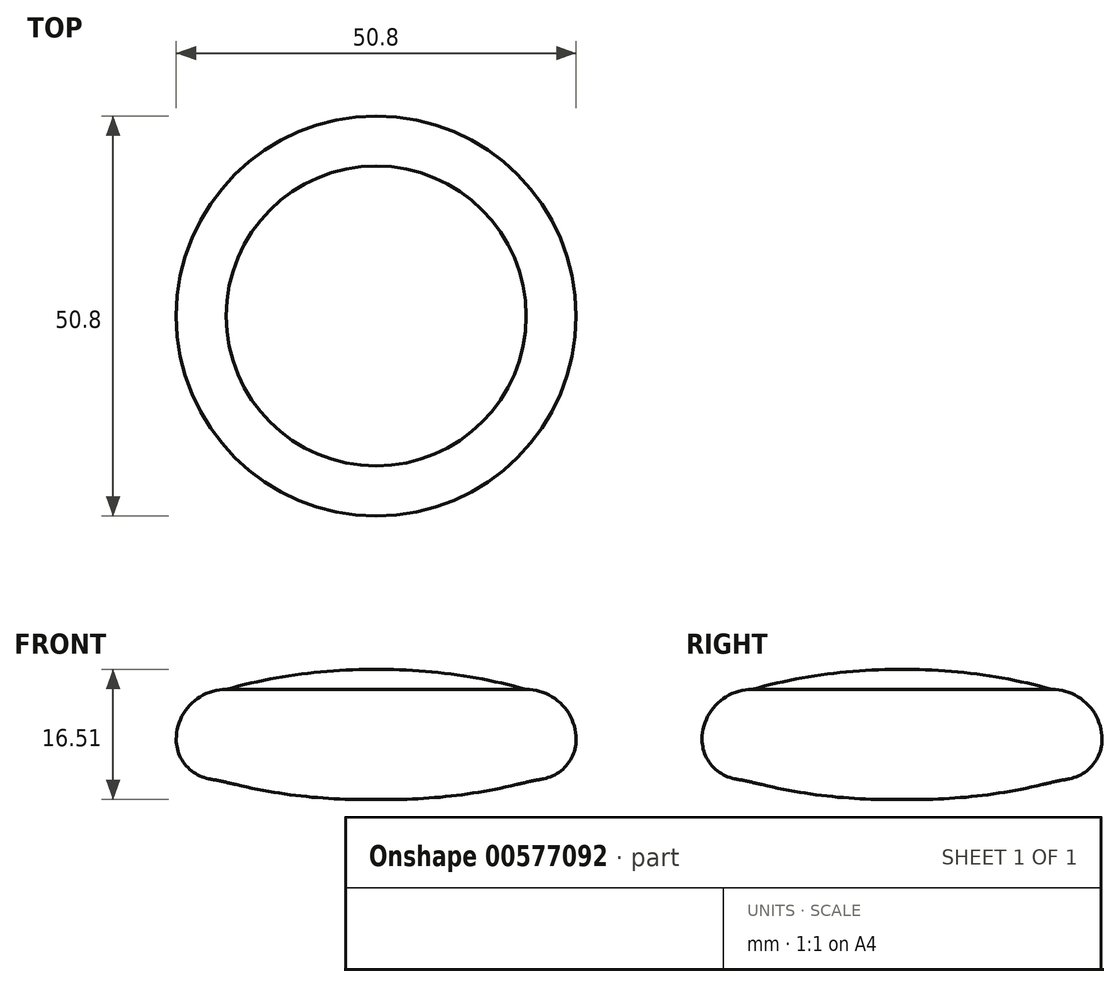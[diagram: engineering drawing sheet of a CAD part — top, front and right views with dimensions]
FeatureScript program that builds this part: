
annotation { "Feature Type Name" : "Feature", "Feature Type Description" : "" }
export const myFeature = defineFeature(function(context is Context, id is Id, definition is map)
    precondition{}
    {
        {
            var Q0;
            Q0=qCreatedBy(makeId("Top.planeOp"),FACE);
            var sketch = newSketch(context, id + "F0", { "sketchPlane" : qUnion([Q0])});
            skCircle(sketch, "E0", {"center": v(0, 0) * mm, "radius": 25.4 * mm});
            skLineSegment(sketch, "E1", {"start": v(-25.4, 0) * mm, "end": v(25.4, 0) * mm});
            skLineSegment(sketch, "E2", {"start": v(0, 25.4) * mm, "end": v(0, -25.4) * mm});
            skSolve(sketch);
        }
        {
            var Q0;
            Q0 = qSketchRegion(id + "F0", true);
            extrude(context, id + "F1", {"entities" : qUnion([Q0]), "depth" : 6.35 * mm, "offsetDistance" : 25.4 * mm});
        }
        {
            var Q0;
            Q0=makeQuery(id+"F1.opExtrude","CAP_EDGE",EDGE,{"disambiguationData":[OSD([sQuery(id+"F0.wireOp",EDGE,"E0")])],"isStart":false});
            fillet(context, id + "F2", {"entities" : qUnion([Q0]), "radius" : 6.35 * mm, "tangentPropagation" : true, "allowEdgeOverflow" : false});
        }
        {
            var Q0;
            Q0=makeQuery(id+"F1.opExtrude","CAP_FACE",FACE,{"disambiguationData":[OSD([sQuery(id+"F0.wireOp",EDGE,"E0")])],"isStart":false});
            extrude(context, id + "F3", {"entities" : qUnion([Q0]), "operationType" : NewBodyOperationType.ADD, "depth" : 2.54 * mm, "offsetDistance" : 25.4 * mm});
        }
        {
            var Q0;
            Q0=makeQuery(id+"F3.opExtrude","CAP_EDGE",EDGE,{"disambiguationData":[OSD([sQuery(id+"F0.wireOp",EDGE,"E0")])],"isStart":false});
            fillet(context, id + "F4", {"entities" : qUnion([Q0]), "radius" : 68.58 * mm, "tangentPropagation" : true, "allowEdgeOverflow" : false});
        }
        {
            var Q0;
            Q0=makeQuery(id+"F1.opExtrude","CAP_FACE",FACE,{"disambiguationData":[OSD([sQuery(id+"F0.wireOp",EDGE,"E0")])],"isStart":true});
            extrude(context, id + "F5", {"entities" : qUnion([Q0]), "operationType" : NewBodyOperationType.ADD, "depth" : 5.08 * mm, "offsetDistance" : 25.4 * mm});
        }
        {
            var Q0;
            Q0=makeQuery(id+"F5.opExtrude","CAP_EDGE",EDGE,{"disambiguationData":[OSD([sQuery(id+"F0.wireOp",EDGE,"E0")])],"isStart":false});
            fillet(context, id + "F6", {"entities" : qUnion([Q0]), "radius" : 5.08 * mm, "tangentPropagation" : true, "allowEdgeOverflow" : false});
        }
        {
            var Q0;
            Q0=makeQuery(id+"F5.opExtrude","CAP_FACE",FACE,{"disambiguationData":[OSD([sQuery(id+"F0.wireOp",EDGE,"E0")])],"isStart":false});
            extrude(context, id + "F7", {"entities" : qUnion([Q0]), "operationType" : NewBodyOperationType.ADD, "depth" : 2.54 * mm, "offsetDistance" : 25.4 * mm});
        }
        {
            var Q0;
            Q0=makeQuery(id+"F7.opExtrude","CAP_EDGE",EDGE,{"disambiguationData":[OSD([sQuery(id+"F0.wireOp",EDGE,"E0")])],"isStart":false});
            fillet(context, id + "F8", {"entities" : qUnion([Q0]), "radius" : 68.58 * mm, "tangentPropagation" : true, "allowEdgeOverflow" : false});
        }
        {
            var Q0;
            {var subQ0=sQuery(id+"F0.wireOp",EDGE,"E0");Q0=makeQuery(id+"F8.opFillet","BLEND_EDGE",EDGE,{"blendedFrom":[makeQuery(id+"F7.opExtrude","CAP_EDGE",EDGE,{"disambiguationData":[OSD([subQ0])],"isStart":false}),makeQuery(id+"F6.opFillet","BLEND_FACE",FACE,{"disambiguationData":[OSD([subQ0])]})],"blendedInto":[makeQuery(id+"F6.opFillet","BLEND_FACE",FACE,{"disambiguationData":[OSD([subQ0])]})]});}
            fillet(context, id + "F9", {"entities" : qUnion([Q0]), "radius" : 73.66 * mm, "tangentPropagation" : true, "allowEdgeOverflow" : false});
        }
    });
